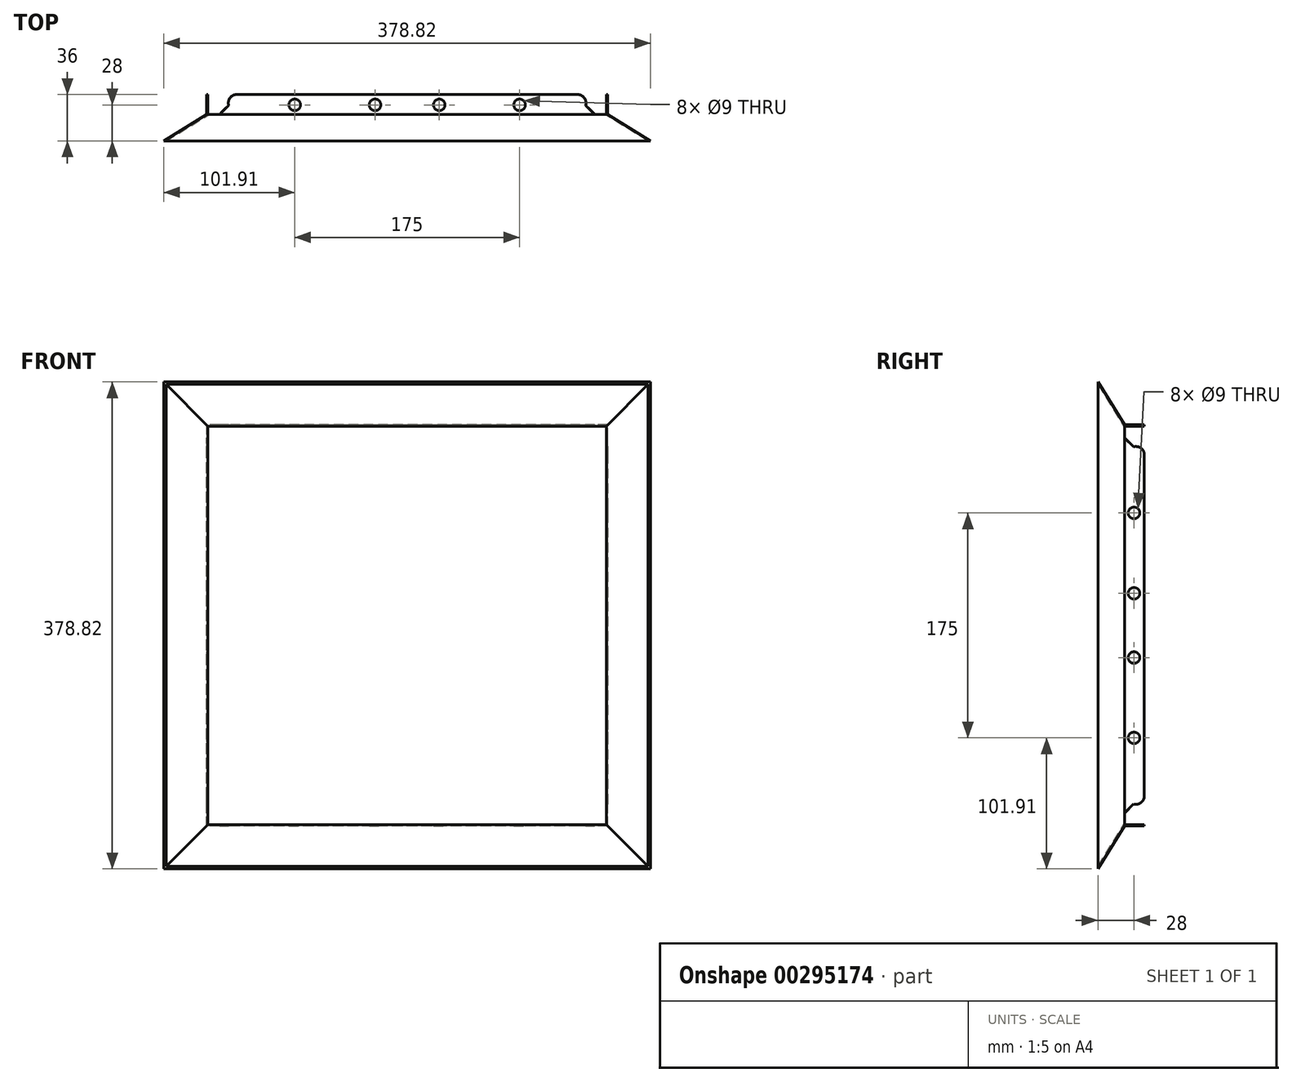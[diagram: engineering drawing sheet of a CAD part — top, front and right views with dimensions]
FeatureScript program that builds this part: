
annotation { "Feature Type Name" : "Feature", "Feature Type Description" : "" }
export const myFeature = defineFeature(function(context is Context, id is Id, definition is map)
    precondition{}
    {
        {
            var Q0;
            Q0=qCreatedBy(makeId("Front.planeOp"),FACE);
            var sketch = newSketch(context, id + "F0", { "sketchPlane" : qUnion([Q0])});
            skLineSegment(sketch, "E0.bottom", {"start": v(192.5, 192.5) * mm, "end": v(-192.5, 192.5) * mm});
            skLineSegment(sketch, "E0.top", {"start": v(192.5, -192.5) * mm, "end": v(-192.5, -192.5) * mm});
            skLineSegment(sketch, "E0.left", {"start": v(192.5, 192.5) * mm, "end": v(192.5, -192.5) * mm});
            skLineSegment(sketch, "E0.right", {"start": v(-192.5, 192.5) * mm, "end": v(-192.5, -192.5) * mm});
            skPoint(sketch, "E0.middle", {"position": v(0, 0) * mm});
            skLineSegment(sketch, "E1.bottom", {"start": v(-187.5, 187.5) * mm, "end": v(187.5, 187.5) * mm});
            skLineSegment(sketch, "E1.top", {"start": v(-187.5, -187.5) * mm, "end": v(187.5, -187.5) * mm});
            skLineSegment(sketch, "E1.left", {"start": v(-187.5, 187.5) * mm, "end": v(-187.5, -187.5) * mm});
            skLineSegment(sketch, "E1.right", {"start": v(187.5, 187.5) * mm, "end": v(187.5, -187.5) * mm});
            skSolve(sketch);
        }
        {
            var Q0;
            Q0=qCreatedBy(makeId("Front.planeOp"),FACE);
            cPlane(context, id + "F1", {"entities" : qUnion([Q0]), "cplaneType" : CPlaneType.OFFSET, "offset" : 20 * mm, "oppositeDirection" : true, "width" : 150 * mm, "height" : 150 * mm});
        }
        {
            var Q0;
            Q0=qCreatedBy(id+"F1.planeOp",FACE);
            var sketch = newSketch(context, id + "F2", { "sketchPlane" : qUnion([Q0])});
            skLineSegment(sketch, "E2.bottom", {"start": v(155, 155) * mm, "end": v(-155, 155) * mm});
            skLineSegment(sketch, "E2.top", {"start": v(155, -155) * mm, "end": v(-155, -155) * mm});
            skLineSegment(sketch, "E2.left", {"start": v(155, 155) * mm, "end": v(155, -155) * mm});
            skLineSegment(sketch, "E2.right", {"start": v(-155, 155) * mm, "end": v(-155, -155) * mm});
            skPoint(sketch, "E2.middle", {"position": v(0, 0) * mm});
            skSolve(sketch);
        }
        {
            var Q0;
            Q0=makeQuery(id+"F0.imprint","IMPRINT",FACE,{"disambiguationData":[TD([[makeQuery(id+"F0.imprint","IMPRINT",EDGE,{"derivedFrom":sQuery(id+"F0.wireOp",EDGE,"E1.bottom")}),-1.0]])]});
            var Q1;
            Q1=makeQuery(id+"F2.imprint","IMPRINT",FACE,{"disambiguationData":[TD([[makeQuery(id+"F2.imprint","IMPRINT",EDGE,{"derivedFrom":sQuery(id+"F2.wireOp",EDGE,"E2.bottom")}),1.0]])]});
            loft(context, id + "F3", {"sheetProfilesArray" : [{ "sheetProfileEntities" : qUnion([Q0]) }, { "sheetProfileEntities" : qUnion([Q1]) }]});
        }
        {
            var Q0;
            Q0=qCreatedBy(id+"F1.planeOp",FACE);
            cPlane(context, id + "F4", {"entities" : qUnion([Q0]), "cplaneType" : CPlaneType.OFFSET, "offset" : 16 * mm, "oppositeDirection" : true, "width" : 150 * mm, "height" : 150 * mm});
        }
        {
            var Q0;
            Q0=qCreatedBy(id+"F4.planeOp",FACE);
            var sketch = newSketch(context, id + "F5", { "sketchPlane" : qUnion([Q0])});
            skLineSegment(sketch, "E3.0.0", {"start": v(155, -155) * mm, "end": v(-155, -155) * mm});
            skLineSegment(sketch, "E3.0.1", {"start": v(-155, -155) * mm, "end": v(-155, 155) * mm});
            skLineSegment(sketch, "E3.0.2", {"start": v(-155, 155) * mm, "end": v(155, 155) * mm});
            skLineSegment(sketch, "E3.0.3", {"start": v(155, 155) * mm, "end": v(155, -155) * mm});
            skSolve(sketch);
        }
        {
            var Q1;
            Q1=makeQuery(id+"F5.imprint","IMPRINT",FACE,{"disambiguationData":[TD([[makeQuery(id+"F5.imprint","IMPRINT",EDGE,{"derivedFrom":sQuery(id+"F5.wireOp",EDGE,"E3.0.0")}),-1.0]])]});
            var Q2;
            Q2=makeQuery(id+"F3.opLoft","CAP_FACE",FACE,{"disambiguationData":[OSD([makeQuery(id+"F2.imprint","IMPRINT",FACE,{"disambiguationData":[TD([[makeQuery(id+"F2.imprint","IMPRINT",EDGE,{"derivedFrom":sQuery(id+"F2.wireOp",EDGE,"E2.bottom")}),1.0]])]})])],"isStart":true});
            loft(context, id + "F6", {"operationType" : NewBodyOperationType.ADD, "sheetProfilesArray" : [{ "sheetProfileEntities" : qUnion([Q1]) }, { "sheetProfileEntities" : qUnion([Q2]) }]});
        }
        {
            var Q0;
            Q0=makeQuery(id+"F3.opLoft","CAP_FACE",FACE,{"disambiguationData":[OSD([makeQuery(id+"F0.imprint","IMPRINT",FACE,{"disambiguationData":[TD([[makeQuery(id+"F0.imprint","IMPRINT",EDGE,{"derivedFrom":sQuery(id+"F0.wireOp",EDGE,"E1.bottom")}),-1.0]])]})])],"isStart":true});
            var Q1;
            Q1=makeQuery(id+"F6.opLoft","CAP_FACE",FACE,{"disambiguationData":[OSD([makeQuery(id+"F5.imprint","IMPRINT",FACE,{"disambiguationData":[TD([[makeQuery(id+"F5.imprint","IMPRINT",EDGE,{"derivedFrom":sQuery(id+"F5.wireOp",EDGE,"E3.0.0")}),-1.0]])]})])],"isStart":true});
            shell(context, id + "F7", {"entities" : qUnion([Q0, Q1]), "thickness" : 1 * mm, "oppositeDirection" : true});
        }
        {
            var Q0;
            Q0=makeQuery(id+"F6.opLoft","SWEPT_FACE",FACE,{"disambiguationData":[OSD([sQuery(id+"F2.wireOp",EDGE,"E2.bottom"),sQuery(id+"F2.wireOp",EDGE,"E2.top"),sQuery(id+"F2.wireOp",EDGE,"E2.right"),sQuery(id+"F5.wireOp",EDGE,"E3.0.0"),sQuery(id+"F5.wireOp",EDGE,"E3.0.1"),sQuery(id+"F5.wireOp",EDGE,"E3.0.2")])]});
            var sketch = newSketch(context, id + "F8", { "sketchPlane" : qUnion([Q0])});
            skLineSegment(sketch, "E4", {"start": v(-20.56, 156) * mm, "end": v(-20.56, 146) * mm});
            skLineSegment(sketch, "E5", {"start": v(-20.56, 146) * mm, "end": v(-27.63, 138.93) * mm});
            skArc(sketch, "E6", {"start": v(-27.63, 138.93) * mm, "mid": v(-33.79, 137.52) * mm, "end": v(-36, 131.6) * mm});
            skLineSegment(sketch, "E7", {"start": v(-20.56, 156) * mm, "end": v(-36, 156) * mm});
            skLineSegment(sketch, "E8", {"start": v(-36, 156) * mm, "end": v(-36, 131.6) * mm});
            skLineSegment(sketch, "E9.MirrorCS", {"start": v(-20.56, -156) * mm, "end": v(-36, -156) * mm});
            skArc(sketch, "E10.MirrorCS", {"start": v(-27.63, -138.93) * mm, "mid": v(-33.79, -137.52) * mm, "end": v(-36, -131.6) * mm});
            skLineSegment(sketch, "E11.MirrorCS", {"start": v(-20.56, -156) * mm, "end": v(-20.56, -146) * mm});
            skLineSegment(sketch, "E12.MirrorCS", {"start": v(-20.56, -146) * mm, "end": v(-27.63, -138.93) * mm});
            skLineSegment(sketch, "E13.MirrorCS", {"start": v(-36, -156) * mm, "end": v(-36, -131.6) * mm});
            skSolve(sketch);
        }
        {
            var Q0;
            Q0=makeQuery(id+"F8.imprint","IMPRINT",FACE,{"disambiguationData":[TD([[makeQuery(id+"F8.imprint","IMPRINT",EDGE,{"derivedFrom":sQuery(id+"F8.wireOp",EDGE,"E4")}),1.0]])]});
            var Q1;
            Q1=sQuery(id+"F8.wireOp",EDGE,"E7");
            revolve(context, id + "F9", {"operationType" : NewBodyOperationType.REMOVE, "entities" : qUnion([Q0]), "axis" : qUnion([Q1]), "revolveType" : RevolveType.FULL, "oppositeDirection" : true});
        }
        {
            var Q0;
            {var subQ4=sQuery(id+"F8.wireOp",EDGE,"E9.MirrorCS");Q0=makeQuery(id+"F8.imprint","IMPRINT",FACE,{"disambiguationData":[TD([[makeQuery(id+"F8.imprint","IMPRINT",EDGE,{"derivedFrom":subQ4}),1.0]])]});}
            var Q1;
            Q1=sQuery(id+"F8.wireOp",EDGE,"E9.MirrorCS");
            revolve(context, id + "F10", {"operationType" : NewBodyOperationType.REMOVE, "entities" : qUnion([Q0]), "axis" : qUnion([Q1]), "revolveType" : RevolveType.FULL, "oppositeDirection" : true});
        }
        {
            var Q0;
            Q0=makeQuery(id+"F6.opLoft","SWEPT_FACE",FACE,{"disambiguationData":[OSD([sQuery(id+"F2.wireOp",EDGE,"E2.bottom"),sQuery(id+"F2.wireOp",EDGE,"E2.top"),sQuery(id+"F2.wireOp",EDGE,"E2.left"),sQuery(id+"F5.wireOp",EDGE,"E3.0.0"),sQuery(id+"F5.wireOp",EDGE,"E3.0.2"),sQuery(id+"F5.wireOp",EDGE,"E3.0.3")])]});
            var sketch = newSketch(context, id + "F11", { "sketchPlane" : qUnion([Q0])});
            skLineSegment(sketch, "E14.0", {"start": v(20.56, -146) * mm, "end": v(27.63, -138.93) * mm});
            skArc(sketch, "E15.0", {"start": v(27.63, -138.93) * mm, "mid": v(33.79, -137.52) * mm, "end": v(36, -131.6) * mm});
            skLineSegment(sketch, "E16.0", {"start": v(20.56, -156) * mm, "end": v(20.56, -146) * mm});
            skLineSegment(sketch, "E17.0", {"start": v(20.56, -156) * mm, "end": v(36, -156) * mm});
            skLineSegment(sketch, "E18.0", {"start": v(36, -156) * mm, "end": v(36, -131.6) * mm});
            skLineSegment(sketch, "E19.MirrorCS", {"start": v(20.56, 156) * mm, "end": v(20.56, 146) * mm});
            skLineSegment(sketch, "E20.MirrorCS", {"start": v(20.56, 156) * mm, "end": v(36, 156) * mm});
            skLineSegment(sketch, "E21.MirrorCS", {"start": v(20.56, 146) * mm, "end": v(27.63, 138.93) * mm});
            skLineSegment(sketch, "E22.MirrorCS", {"start": v(36, 156) * mm, "end": v(36, 131.6) * mm});
            skArc(sketch, "E23.MirrorCS", {"start": v(27.63, 138.93) * mm, "mid": v(33.79, 137.52) * mm, "end": v(36, 131.6) * mm});
            skSolve(sketch);
        }
        {
            var Q0;
            {var subQ2=sQuery(id+"F11.wireOp",EDGE,"E14.0");Q0=makeQuery(id+"F11.imprint","IMPRINT",FACE,{"disambiguationData":[TD([[makeQuery(id+"F11.imprint","IMPRINT",EDGE,{"derivedFrom":subQ2}),-1.0]])]});}
            var Q1;
            Q1=sQuery(id+"F11.wireOp",EDGE,"E17.0");
            revolve(context, id + "F12", {"operationType" : NewBodyOperationType.REMOVE, "entities" : qUnion([Q0]), "axis" : qUnion([Q1]), "revolveType" : RevolveType.FULL, "oppositeDirection" : true});
        }
        {
            var Q0;
            Q0=makeQuery(id+"F11.imprint","IMPRINT",FACE,{"disambiguationData":[TD([[makeQuery(id+"F11.imprint","IMPRINT",EDGE,{"derivedFrom":sQuery(id+"F11.wireOp",EDGE,"E19.MirrorCS")}),1.0]])]});
            var Q1;
            Q1=sQuery(id+"F11.wireOp",EDGE,"E20.MirrorCS");
            revolve(context, id + "F13", {"operationType" : NewBodyOperationType.REMOVE, "entities" : qUnion([Q0]), "axis" : qUnion([Q1]), "revolveType" : RevolveType.FULL, "oppositeDirection" : true});
        }
        {
            var Q0;
            Q0=makeQuery(id+"F6.opLoft","SWEPT_FACE",FACE,{"disambiguationData":[OSD([sQuery(id+"F2.wireOp",EDGE,"E2.top"),sQuery(id+"F2.wireOp",EDGE,"E2.left"),sQuery(id+"F2.wireOp",EDGE,"E2.right"),sQuery(id+"F5.wireOp",EDGE,"E3.0.0"),sQuery(id+"F5.wireOp",EDGE,"E3.0.1"),sQuery(id+"F5.wireOp",EDGE,"E3.0.3")])]});
            var sketch = newSketch(context, id + "F14", { "sketchPlane" : qUnion([Q0])});
            skCircle(sketch, "E24", {"center": v(-25, -28) * mm, "radius": 4.5 * mm});
            skCircle(sketch, "E25", {"center": v(25, -28) * mm, "radius": 4.5 * mm});
            skCircle(sketch, "E26", {"center": v(-87.5, -28) * mm, "radius": 4.5 * mm});
            skCircle(sketch, "E27", {"center": v(87.5, -28) * mm, "radius": 4.5 * mm});
            skSolve(sketch);
        }
        {
            var Q0;
            Q0=qSketchRegion(id+"F14",true);
            extrude(context, id + "F15", {"entities" : qUnion([Q0]), "operationType" : NewBodyOperationType.REMOVE, "endBound" : BoundingType.THROUGH_ALL, "oppositeDirection" : true, "depth" : 25 * mm});
        }
        {
            var Q0;
            Q0=makeQuery(id+"F6.opLoft","SWEPT_FACE",FACE,{"disambiguationData":[OSD([sQuery(id+"F2.wireOp",EDGE,"E2.bottom"),sQuery(id+"F2.wireOp",EDGE,"E2.top"),sQuery(id+"F2.wireOp",EDGE,"E2.right"),sQuery(id+"F5.wireOp",EDGE,"E3.0.0"),sQuery(id+"F5.wireOp",EDGE,"E3.0.1"),sQuery(id+"F5.wireOp",EDGE,"E3.0.2")])]});
            var sketch = newSketch(context, id + "F16", { "sketchPlane" : qUnion([Q0])});
            skCircle(sketch, "E28", {"center": v(-28, 25) * mm, "radius": 4.5 * mm});
            skCircle(sketch, "E29", {"center": v(-28, 87.5) * mm, "radius": 4.5 * mm});
            skCircle(sketch, "E30.MirrorC", {"center": v(-28, -25) * mm, "radius": 4.5 * mm});
            skCircle(sketch, "E31.MirrorC", {"center": v(-28, -87.5) * mm, "radius": 4.5 * mm});
            skSolve(sketch);
        }
        {
            var Q0;
            Q0=qSketchRegion(id+"F16",true);
            extrude(context, id + "F17", {"entities" : qUnion([Q0]), "operationType" : NewBodyOperationType.REMOVE, "endBound" : BoundingType.THROUGH_ALL, "oppositeDirection" : true, "depth" : 25 * mm});
        }
    });
